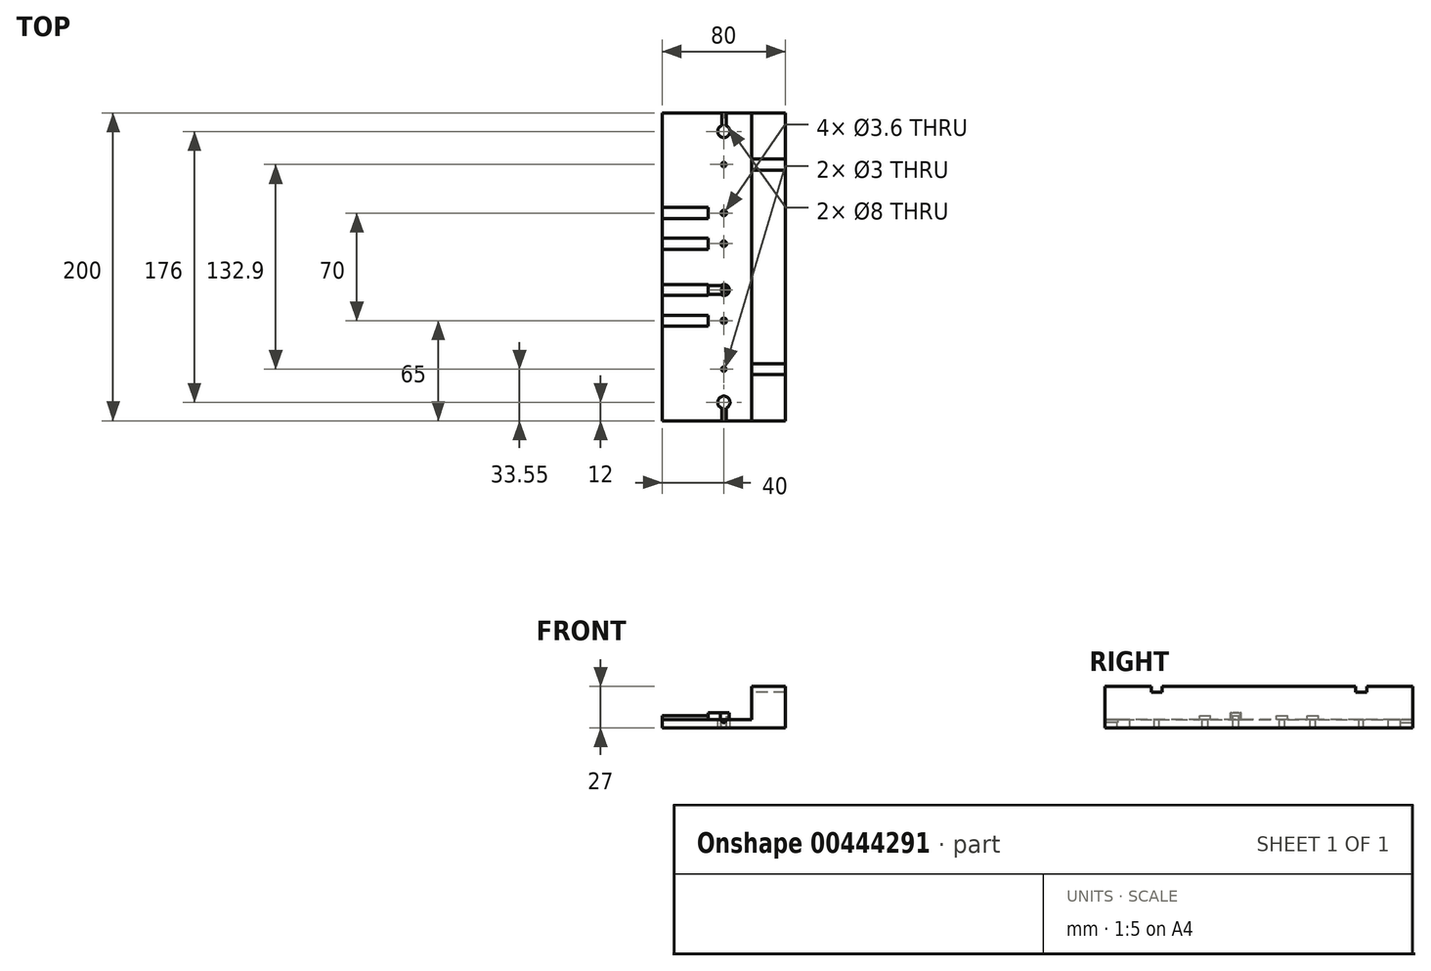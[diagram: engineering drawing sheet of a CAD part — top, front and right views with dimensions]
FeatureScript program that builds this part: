
annotation { "Feature Type Name" : "Feature", "Feature Type Description" : "" }
export const myFeature = defineFeature(function(context is Context, id is Id, definition is map)
    precondition{}
    {
        {
            var Q0;
            Q0=qCreatedBy(makeId("Top.planeOp"),FACE);
            var sketch = newSketch(context, id + "F0", { "sketchPlane" : qUnion([Q0])});
            skLineSegment(sketch, "E0.bottom", {"start": v(40, -100) * mm, "end": v(-40, -100) * mm});
            skLineSegment(sketch, "E0.top", {"start": v(40, 100) * mm, "end": v(-40, 100) * mm});
            skLineSegment(sketch, "E0.left", {"start": v(40, -100) * mm, "end": v(40, 100) * mm});
            skLineSegment(sketch, "E0.right", {"start": v(-40, -100) * mm, "end": v(-40, 100) * mm});
            skPoint(sketch, "E0.middle", {"position": v(0, 0) * mm});
            skCircle(sketch, "E1", {"center": v(0, 15) * mm, "radius": 1.8 * mm});
            skCircle(sketch, "E2", {"center": v(0, 88) * mm, "radius": 4 * mm});
            skCircle(sketch, "E3.MirrorC", {"center": v(0, -88) * mm, "radius": 4 * mm});
            skLineSegment(sketch, "E4", {"start": v(18, 100) * mm, "end": v(18, -100) * mm});
            skLineSegment(sketch, "E5", {"start": v(40, 70) * mm, "end": v(18, 70) * mm});
            skLineSegment(sketch, "E6", {"start": v(40, 62.9) * mm, "end": v(18, 62.9) * mm});
            skLineSegment(sketch, "E7.MirrorCS", {"start": v(40, -62.9) * mm, "end": v(18, -62.9) * mm});
            skLineSegment(sketch, "E8.MirrorCS", {"start": v(40, -70) * mm, "end": v(18, -70) * mm});
            skLineSegment(sketch, "E9", {"start": v(0, 15) * mm, "end": v(-35.5, 15) * mm, "construction": true});
            skLineSegment(sketch, "E10", {"start": v(0, 35) * mm, "end": v(-35.5, 35) * mm, "construction": true});
            skArc(sketch, "E11", {"start": v(-2.32, 32.25) * mm, "mid": v(3.6, 35) * mm, "end": v(-2.32, 37.75) * mm});
            skCircle(sketch, "E12", {"center": v(0, 35) * mm, "radius": 1.8 * mm});
            skLineSegment(sketch, "E13", {"start": v(-40, 38.55) * mm, "end": v(-10.32, 38.55) * mm});
            skLineSegment(sketch, "E14", {"start": v(-2.32, 37.75) * mm, "end": v(-10.32, 37.75) * mm});
            skLineSegment(sketch, "E15.MirrorCS", {"start": v(-2.32, 32.25) * mm, "end": v(-10.32, 32.25) * mm});
            skLineSegment(sketch, "E16.MirrorCS", {"start": v(-40, 31.45) * mm, "end": v(-10.32, 31.45) * mm});
            skLineSegment(sketch, "E17", {"start": v(-10.32, 38.55) * mm, "end": v(-10.32, 37.75) * mm});
            skArc(sketch, "E18", {"start": v(-2.32, 12.25) * mm, "mid": v(3.6, 15) * mm, "end": v(-2.32, 17.75) * mm});
            skLineSegment(sketch, "E19", {"start": v(-2.32, 17.75) * mm, "end": v(-10.32, 17.75) * mm});
            skLineSegment(sketch, "E20", {"start": v(-10.32, 18.55) * mm, "end": v(-40, 18.55) * mm});
            skLineSegment(sketch, "E21.MirrorCS", {"start": v(-2.32, 12.25) * mm, "end": v(-10.32, 12.25) * mm});
            skLineSegment(sketch, "E22.MirrorCS", {"start": v(-10.32, 11.45) * mm, "end": v(-40, 11.45) * mm});
            skLineSegment(sketch, "E23.trimOffspring", {"start": v(-10.32, 32.25) * mm, "end": v(-10.32, 31.45) * mm});
            skLineSegment(sketch, "E24.trimOffspring", {"start": v(-10.32, 18.55) * mm, "end": v(-10.32, 17.75) * mm});
            skArc(sketch, "E25.MirrorC", {"start": v(-2.32, -12.25) * mm, "mid": v(3.6, -15) * mm, "end": v(-2.32, -17.75) * mm});
            skCircle(sketch, "E26.MirrorC", {"center": v(0, -15) * mm, "radius": 1.8 * mm});
            skLineSegment(sketch, "E27.MirrorCS", {"start": v(-2.32, -17.75) * mm, "end": v(-10.32, -17.75) * mm});
            skLineSegment(sketch, "E28.MirrorCS", {"start": v(-2.32, -12.25) * mm, "end": v(-10.32, -12.25) * mm});
            skLineSegment(sketch, "E29.MirrorCS", {"start": v(-10.32, -18.55) * mm, "end": v(-10.32, -17.75) * mm});
            skLineSegment(sketch, "E30.MirrorCS", {"start": v(-10.32, -11.45) * mm, "end": v(-40, -11.45) * mm});
            skLineSegment(sketch, "E31.MirrorCS", {"start": v(-10.32, -18.55) * mm, "end": v(-40, -18.55) * mm});
            skLineSegment(sketch, "E32.MirrorCS", {"start": v(-2.32, -32.25) * mm, "end": v(-10.32, -32.25) * mm});
            skCircle(sketch, "E33.MirrorC", {"center": v(0, -35) * mm, "radius": 1.8 * mm});
            skArc(sketch, "E34.MirrorCS", {"start": v(-2.32, -32.25) * mm, "mid": v(3.6, -35) * mm, "end": v(-2.32, -37.75) * mm});
            skLineSegment(sketch, "E35.MirrorCS", {"start": v(-2.32, -37.75) * mm, "end": v(-10.32, -37.75) * mm});
            skLineSegment(sketch, "E36.MirrorCS", {"start": v(-40, -38.55) * mm, "end": v(-10.32, -38.55) * mm});
            skLineSegment(sketch, "E37.MirrorCS", {"start": v(-40, -31.45) * mm, "end": v(-10.32, -31.45) * mm});
            skLineSegment(sketch, "E38.MirrorCS", {"start": v(-10.32, -32.25) * mm, "end": v(-10.32, -31.45) * mm});
            skLineSegment(sketch, "E39.MirrorCS", {"start": v(-10.32, -38.55) * mm, "end": v(-10.32, -37.75) * mm});
            skLineSegment(sketch, "E40.trimOffspring", {"start": v(-10.32, 12.25) * mm, "end": v(-10.32, 11.45) * mm});
            skLineSegment(sketch, "E41.trimOffspring", {"start": v(-10.32, -12.25) * mm, "end": v(-10.32, -11.45) * mm});
            skLineSegment(sketch, "E42", {"start": v(-10.32, 37.75) * mm, "end": v(-10.32, 32.25) * mm});
            skLineSegment(sketch, "E43", {"start": v(-10.32, 17.75) * mm, "end": v(-10.32, 12.25) * mm});
            skLineSegment(sketch, "E44", {"start": v(-10.32, -12.25) * mm, "end": v(-10.32, -17.75) * mm});
            skLineSegment(sketch, "E45", {"start": v(-10.32, -32.25) * mm, "end": v(-10.32, -37.75) * mm});
            skCircle(sketch, "E46", {"center": v(0, 66.45) * mm, "radius": 1.5 * mm});
            skCircle(sketch, "E47.MirrorC", {"center": v(0, -66.45) * mm, "radius": 1.5 * mm});
            skSolve(sketch);
        }
        {
            var Q0;
            Q0 = qSketchRegion(id + "F0", true);
            var Q1;
            Q1=makeQuery(id+"F0.imprint","IMPRINT",FACE,{"disambiguationData":[TD([[makeQuery(id+"F0.imprint","IMPRINT",EDGE,{"derivedFrom":sQuery(id+"F0.wireOp",EDGE,"63ea390f-9383-4d79-a431-791635a6dfa00.MirrorC")}),1.0]])]});
            var Q2;
            Q2=makeQuery(id+"F0.imprint","IMPRINT",FACE,{"disambiguationData":[TD([[makeQuery(id+"F0.imprint","IMPRINT",EDGE,{"derivedFrom":sQuery(id+"F0.wireOp",EDGE,"E1")}),-1.0]])]});
            var Q3;
            Q3=makeQuery(id+"F0.imprint","IMPRINT",FACE,{"disambiguationData":[TD([[makeQuery(id+"F0.imprint","IMPRINT",EDGE,{"derivedFrom":sQuery(id+"F0.wireOp",EDGE,"849a979c-cdea-47ef-98aa-30cc51323e3e0.MirrorCS")}),-1.0]])]});
            var Q4;
            Q4=makeQuery(id+"F0.imprint","IMPRINT",FACE,{"disambiguationData":[TD([[makeQuery(id+"F0.imprint","IMPRINT",EDGE,{"derivedFrom":sQuery(id+"F0.wireOp",EDGE,"84a13eab-ef58-4a5a-8f90-f34b747f32890.MirrorCS")}),1.0]])]});
            var Q5;
            Q5=makeQuery(id+"F0.imprint","IMPRINT",FACE,{"disambiguationData":[TD([[makeQuery(id+"F0.imprint","IMPRINT",EDGE,{"derivedFrom":sQuery(id+"F0.wireOp",EDGE,"dae8b242-f5bc-4362-89cb-ea1d936c60dd0.MirrorC")}),-1.0]])]});
            var Q6;
            Q6=makeQuery(id+"F0.imprint","IMPRINT",FACE,{"disambiguationData":[TD([[makeQuery(id+"F0.imprint","IMPRINT",EDGE,{"derivedFrom":sQuery(id+"F0.wireOp",EDGE,"E11")}),1.0]])]});
            var Q7;
            {var subQ0=sQuery(id+"F0.wireOp",EDGE,"E27.MirrorCS");Q7=makeQuery(id+"F0.imprint","IMPRINT",FACE,{"disambiguationData":[TD([[makeQuery(id+"F0.imprint","IMPRINT",EDGE,{"derivedFrom":subQ0}),-1.0]])]});}
            var Q8;
            Q8=makeQuery(id+"F0.imprint","IMPRINT",FACE,{"disambiguationData":[TD([[makeQuery(id+"F0.imprint","IMPRINT",EDGE,{"derivedFrom":sQuery(id+"F0.wireOp",EDGE,"E32.MirrorCS")}),1.0]])]});
            extrude(context, id + "F1", {"entities" : qUnion([Q0, Q1, Q2, Q3, Q4, Q5, Q6, Q7, Q8]), "oppositeDirection" : true, "depth" : 10 * mm});
        }
        {
            var Q0;
            Q0=makeQuery(id+"F0.imprint","IMPRINT",FACE,{"disambiguationData":[TD([[makeQuery(id+"F0.imprint","IMPRINT",EDGE,{"derivedFrom":sQuery(id+"F0.wireOp",EDGE,"E32.MirrorCS")}),1.0]])]});
            var Q1;
            Q1=makeQuery(id+"F0.imprint","IMPRINT",FACE,{"disambiguationData":[TD([[makeQuery(id+"F0.imprint","IMPRINT",EDGE,{"derivedFrom":sQuery(id+"F0.wireOp",EDGE,"E25.MirrorC")}),-1.0]])]});
            var Q2;
            Q2=makeQuery(id+"F0.imprint","IMPRINT",FACE,{"disambiguationData":[TD([[makeQuery(id+"F0.imprint","IMPRINT",EDGE,{"derivedFrom":sQuery(id+"F0.wireOp",EDGE,"E1")}),-1.0]])]});
            var Q3;
            Q3=makeQuery(id+"F0.imprint","IMPRINT",FACE,{"disambiguationData":[TD([[makeQuery(id+"F0.imprint","IMPRINT",EDGE,{"derivedFrom":sQuery(id+"F0.wireOp",EDGE,"E11")}),1.0]])]});
            extrude(context, id + "F2", {"entities" : qUnion([Q0, Q1, Q2, Q3]), "operationType" : NewBodyOperationType.REMOVE, "oppositeDirection" : true, "depth" : 4.5 * mm});
        }
        {
            var Q0;
            {var subQ5=sQuery(id+"F0.wireOp",EDGE,"E8.MirrorCS");Q0=makeQuery(id+"F0.imprint","IMPRINT",FACE,{"disambiguationData":[TD([[makeQuery(id+"F0.imprint","IMPRINT",EDGE,{"derivedFrom":subQ5}),1.0]])]});}
            var Q1;
            {var subQ5=sQuery(id+"F0.wireOp",EDGE,"E5");Q1=makeQuery(id+"F0.imprint","IMPRINT",FACE,{"disambiguationData":[TD([[makeQuery(id+"F0.imprint","IMPRINT",EDGE,{"derivedFrom":subQ5}),-1.0]])]});}
            var Q2;
            {var subQ0=sQuery(id+"F0.wireOp",EDGE,"E6");Q2=makeQuery(id+"F0.imprint","IMPRINT",FACE,{"disambiguationData":[TD([[makeQuery(id+"F0.imprint","IMPRINT",EDGE,{"derivedFrom":subQ0}),1.0]])]});}
            extrude(context, id + "F3", {"entities" : qUnion([Q0, Q1, Q2]), "operationType" : NewBodyOperationType.ADD, "depth" : 17 * mm});
        }
        {
            var Q0;
            {var subQ0=sQuery(id+"F0.wireOp",EDGE,"E5");Q0=makeQuery(id+"F0.imprint","IMPRINT",FACE,{"disambiguationData":[TD([[makeQuery(id+"F0.imprint","IMPRINT",EDGE,{"derivedFrom":subQ0}),1.0]])]});}
            var Q1;
            {var subQ0=sQuery(id+"F0.wireOp",EDGE,"E7.MirrorCS");Q1=makeQuery(id+"F0.imprint","IMPRINT",FACE,{"disambiguationData":[TD([[makeQuery(id+"F0.imprint","IMPRINT",EDGE,{"derivedFrom":subQ0}),1.0]])]});}
            extrude(context, id + "F4", {"entities" : qUnion([Q0, Q1]), "operationType" : NewBodyOperationType.ADD, "depth" : 13.2 * mm});
        }
        {
            var Q0;
            {var subQ0=sQuery(id+"F0.wireOp",EDGE,"E0.top");Q0=makeQuery(id+"F3.boolean.opBoolean","MERGE",FACE,{"derivedFrom":[makeQuery(id+"F1.opExtrude","SWEPT_FACE",FACE,{"disambiguationData":[OSD([subQ0])]}),makeQuery(id+"F3.opExtrude","SWEPT_FACE",FACE,{"disambiguationData":[OSD([subQ0])]})]});}
            var sketch = newSketch(context, id + "F5", { "sketchPlane" : qUnion([Q0])});
            skCircle(sketch, "E48", {"center": v(0, -5) * mm, "radius": 1.5 * mm});
            skSolve(sketch);
        }
        {
            var Q0;
            Q0=makeQuery(id+"F5.imprint","IMPRINT",FACE,{"disambiguationData":[TD([[makeQuery(id+"F5.imprint","IMPRINT",EDGE,{"derivedFrom":sQuery(id+"F5.wireOp",EDGE,"E48")}),1.0]])]});
            extrude(context, id + "F6", {"entities" : qUnion([Q0]), "operationType" : NewBodyOperationType.REMOVE, "oppositeDirection" : true, "depth" : 15 * mm});
        }
        {
            var Q0;
            {var subQ0=sQuery(id+"F0.wireOp",EDGE,"E0.bottom");Q0=makeQuery(id+"F3.boolean.opBoolean","MERGE",FACE,{"derivedFrom":[makeQuery(id+"F1.opExtrude","SWEPT_FACE",FACE,{"disambiguationData":[OSD([subQ0])]}),makeQuery(id+"F3.opExtrude","SWEPT_FACE",FACE,{"disambiguationData":[OSD([subQ0])]})]});}
            var sketch = newSketch(context, id + "F7", { "sketchPlane" : qUnion([Q0])});
            skCircle(sketch, "E49", {"center": v(0, -5) * mm, "radius": 1.5 * mm});
            skSolve(sketch);
        }
        {
            var Q0;
            Q0=makeQuery(id+"F7.imprint","IMPRINT",FACE,{"disambiguationData":[TD([[makeQuery(id+"F7.imprint","IMPRINT",EDGE,{"derivedFrom":sQuery(id+"F7.wireOp",EDGE,"E49")}),1.0]])]});
            extrude(context, id + "F8", {"entities" : qUnion([Q0]), "operationType" : NewBodyOperationType.REMOVE, "oppositeDirection" : true, "depth" : 15 * mm});
        }
        {
            var Q0;
            {var subQ1=sQuery(id+"F0.wireOp",EDGE,"E13");Q0=makeQuery(id+"F0.imprint","IMPRINT",FACE,{"disambiguationData":[TD([[makeQuery(id+"F0.imprint","IMPRINT",EDGE,{"derivedFrom":subQ1}),-1.0]])]});}
            var Q1;
            {var subQ1=sQuery(id+"F0.wireOp",EDGE,"E20");Q1=makeQuery(id+"F0.imprint","IMPRINT",FACE,{"disambiguationData":[TD([[makeQuery(id+"F0.imprint","IMPRINT",EDGE,{"derivedFrom":subQ1}),1.0]])]});}
            var Q2;
            Q2=makeQuery(id+"F0.imprint","IMPRINT",FACE,{"disambiguationData":[TD([[makeQuery(id+"F0.imprint","IMPRINT",EDGE,{"derivedFrom":sQuery(id+"F0.wireOp",EDGE,"E29.MirrorCS")}),1.0]])]});
            var Q3;
            {var subQ1=sQuery(id+"F0.wireOp",EDGE,"E36.MirrorCS");Q3=makeQuery(id+"F0.imprint","IMPRINT",FACE,{"disambiguationData":[TD([[makeQuery(id+"F0.imprint","IMPRINT",EDGE,{"derivedFrom":subQ1}),1.0]])]});}
            extrude(context, id + "F9", {"entities" : qUnion([Q0, Q1, Q2, Q3]), "operationType" : NewBodyOperationType.REMOVE, "oppositeDirection" : true, "depth" : 2 * mm});
        }
    });
